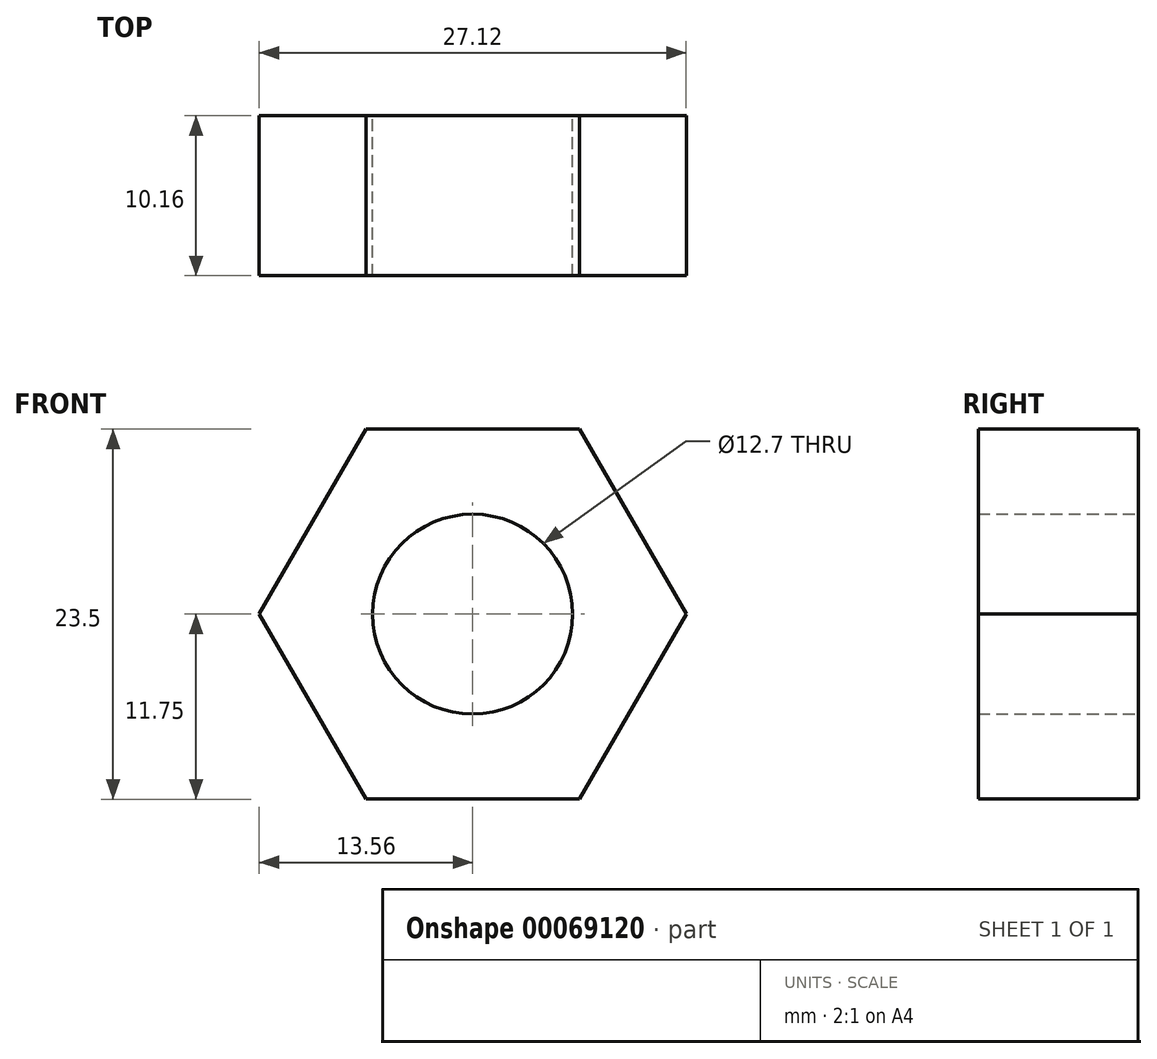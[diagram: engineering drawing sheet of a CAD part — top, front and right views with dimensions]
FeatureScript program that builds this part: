
annotation { "Feature Type Name" : "Feature", "Feature Type Description" : "" }
export const myFeature = defineFeature(function(context is Context, id is Id, definition is map)
    precondition{}
    {
        {
            var Q0;
            Q0=qCreatedBy(makeId("Front.planeOp"),FACE);
            var sketch = newSketch(context, id + "F0", { "sketchPlane" : qUnion([Q0])});
            skCircle(sketch, "E0.cCircle", {"center": v(0, 0) * mm, "radius": 11.75 * mm, "construction": true});
            skLineSegment(sketch, "E0.0", {"start": v(6.78, -11.75) * mm, "end": v(-6.78, -11.75) * mm});
            skLineSegment(sketch, "E0.1", {"start": v(-6.78, -11.75) * mm, "end": v(-13.56, 0) * mm});
            skLineSegment(sketch, "E0.2", {"start": v(-13.56, 0) * mm, "end": v(-6.78, 11.75) * mm});
            skLineSegment(sketch, "E0.3", {"start": v(-6.78, 11.75) * mm, "end": v(6.78, 11.75) * mm});
            skLineSegment(sketch, "E0.4", {"start": v(6.78, 11.75) * mm, "end": v(13.56, 0) * mm});
            skLineSegment(sketch, "E0.5", {"start": v(13.56, 0) * mm, "end": v(6.78, -11.75) * mm});
            skPoint(sketch, "E0.0.midPoint", {"position": v(0, -11.75) * mm});
            skCircle(sketch, "E1", {"center": v(0, 0) * mm, "radius": 6.35 * mm});
            skSolve(sketch);
        }
        {
            var Q0;
            Q0=makeQuery(id+"F0.imprint","IMPRINT",FACE,{"disambiguationData":[TD([[makeQuery(id+"F0.imprint","IMPRINT",EDGE,{"derivedFrom":sQuery(id+"F0.wireOp",EDGE,"E0.0")}),-1.0]])]});
            extrude(context, id + "F1", {"entities" : qUnion([Q0]), "depth" : 10.16 * mm});
        }
    });
